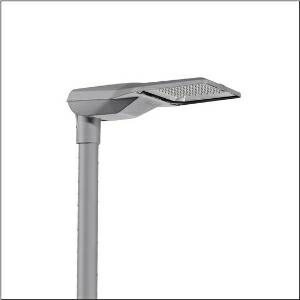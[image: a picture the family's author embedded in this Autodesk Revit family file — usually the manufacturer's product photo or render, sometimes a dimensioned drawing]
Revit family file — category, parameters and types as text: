
# Revit family: streetlight_sl_21_iq_midi___pl52_5xe3h41g08mb_9f92
name_source: partatom
category: Lighting Fixtures
units: mm (PartAtom-declared; Revit-internal decimal feet)

## family parameters
Cut with Voids When Loaded = No
Host = Face
Light Source = No
Part Type = Normal
Room Calculation Point = No
Round Connector Dimension = Use Diameter
Shared = No

## types (1)
- --- (1 x LED, 20000 lm, 146.7 W, 4000K)
    Apparent Load = 147 VA
    CIE Flux Codes = 27 59 98 100 100
    Color Rendering = 70
    Color Temperature = 4000K
    Default Elevation = 1800 mm
    Description = Streetlight SL 21 iQ midi, mast luminaire, primary light control with lens, of PMMA, primary optical cover: cover, of toughened safety glass, transparent, light distribution: PL52, light emission: direct distribution, primary light characteristic: asymmetric, installation type: post-top, side-entry, LED, High Power LED, rated luminous flux: 20.000lm, luminous efficacy: 136lm/W, light colour: 740, colour temperature: 4000K, control gear: iQ Street-Remote, control: Street-Remote, Auto-Match, Temp-Guard, Lumen-Switch, Night-Set, Smart-Wire, Light-Fading, Desk-Remote (wireless, voltage-free reading and setting of iQ features in the workshop via application-optimized NFC function/RFID function), optimised constant luminous flux control (CLO 2.0), pre-setting: linear dimming characteristic, mains connection: 230..240V, AC, 50/60Hz, start of lifetime: 147W, end of service life: 161W, reduction: 62W, luminaire housing, of diecast aluminium, powder-coated, SITECO metallic grey (DB 702S), corrosivity category C5 high according to DIN EN ISO 12944, please order mast flange separately, inclination adjustable: 0°, 5°, 10°, 15°, sealing non-destructively replaceable, multi-level sealing system, length: 644mm, width: 335mm, height: 110mm, mast flange for spigot size: 42mm (side-entry): 5XC10008XM4, 60/48mm (side-entry/post-top): 5XC10108XM2, 76/60mm (side-entry/post-top): 5XC10108XM1, mounting height: 4..8m, protection rating (complete): IP66, insulation class (complete): insulation class II (safety insulation), certification: CE, ENEC, ENEC+, VDE, impact resistance: IK10, permissible operating ambient temperature for outdoor applications: -40..+50°C, standard-compliant lighting for roads and squares, packaging unit: 1 piece

Light Distribution: PL52
    Height = 111 mm
    Lamp = 1 x LED
    Lamp Light Flux = 20000 lm
    Lamp Power = 146.7 W
    Lamp count = 1
    Length = 644 mm
    Luminous efficacy = 136 lm/W
    Manufacturer = Siteco
    ModVariant = No
    Model = 5XE3H41G08MB
    Number of Poles = 1
    OnlyDefault = Yes
    Power Factor = 1
    Product Name = Streetlight SL 21 iQ midi | PL52
    Product group = mast luminaire | pylon top
    ProductGroupID = 6100
    Protection Class = Protection class II
    Protection Degree = IP 66
    RLX_Detail_Level = 1
    RLX_Emergency_Light_Flux = 0 lm
    RLX_Emergency_Type = 0
    RLX_Emergency_Type_DB = No
    RlxData = <blob elided: 36549 chars, md5=13de37bb>
    Socket = socket
    Standby Power = 0 W
    System Light Flux = 20000 lm
    System Power = 147 W
    Type Comments = factory setting: luminous flux: 100 % | dim-lin: 254 | 753 mA
    Type Image = l_1004298.jpg
    URL = http://relux.com
    VarID = @adj_188167
    Voltage = 0 V
    Weight = 0.00 kg
    Width = 336 mm

## geometry (parser evidence)
native form markers: Blend x4, Sweep x10
no freeform markers — native parametric forms only
